MODEL slx_756ac407c6a5
KIND model
CONFIG AbsTol = auto
CONFIG EnableMultiTasking = off
CONFIG FixedStep = SimIn.Environment.Turbulence.dT
CONFIG MaxStep = auto
CONFIG MinStep = auto
CONFIG RelTol = 1e-6
CONFIG SampleTimeConstraint = Unconstrained
CONFIG SolverName = FixedStepAuto
CONFIG StartTime = 0.0
CONFIG StopTime = SimIn.stopTime
BLOCK [SubSystem] Assertions
BLOCK [Clock] Assertions/Clock1
BLOCK [Reference] Assertions/Compare To Constant  REF=simulink/Logic and Bit
Operations/Compare
To Constant
  SourceBlock = simulink/Logic and Bit\nOperations/Compare\nTo Constant
  SourceType = Compare To Constant
BLOCK [Constant] Assertions/Constant2
  Value = SimIn.Switches.TrimModeOn
BLOCK [Constant] Assertions/Constant3
  Value = SimIn.Switches.LinearizeModeOn
BLOCK [Assertion] Assertions/KillifNotSimMode
  AssertionFailFcn = warndlg('Running simulation with TrimMode or LinearizeMode engaged.  Run setup.m to reset.','Warning!')
BLOCK [Logic] Assertions/Logical Operator
  AllPortsSameDT = off
  Operator = NAND
  OutDataTypeStr = boolean
BLOCK [Logic] Assertions/Logical Operator1
  AllPortsSameDT = off
  Operator = OR
  OutDataTypeStr = boolean
BLOCK [BusCreator] Bus Creator
  DisplayOption = bar
  InheritFromInputs = on
  Inputs = 2
  OutDataTypeStr = Bus: BUS_TRIM_INPUT
BLOCK [BusSelector] Bus Selector
  OutputSignals = Vehicle.EOM
BLOCK [BusSelector] Bus Selector1
  OutputAsBus = on
  OutputSignals = AirRelativeData.Veas,AirRelativeData.Vtot,AirRelativeData.alpha,AirRelativeData.beta,WorldRelativeData.gamma,WorldRelativeData.chi,InertialData.Asensed_bIb,AirRelativeData.Vtotdot,AirRelativeData.alphadot,AirRelativeData.betadot,WorldRelativeData.gammadot,WorldRelativeData.chidot,WorldRelativeData.VelDtH_bEh,WorldRelativeData.Euler.phi,WorldRelativeData.Euler.theta,WorldRelativeData.Euler.psi
BLOCK [BusSelector] Bus Selector2
  OutputSignals = InertialData.Pos_bii
BLOCK [BusSelector] Bus Selector5
  OutputSignals = Vehicle.EOM.WorldRelativeData.LatLonAlt.Lon,Vehicle.EOM.WorldRelativeData.LatLonAlt.LatGeod,Vehicle.EOM.WorldRelativeData.LatLonAlt.AltGeod,Vehicle.EOM.WorldRelativeData.Euler,Vehicle.EOM.AirRelativeData.Vcas,Vehicle.EOM.WorldRelativeData.Vel_bEh,Vehicle.EOM.InertialData.Accel_bIi,Vehicle.EOM.WorldRelativeData.AltAGL
BLOCK [BusToVector] Bus to Vector
BLOCK [Demux] Demux
  Outputs = [SimIn.Trim.numEngines SimIn.Trim.numSurfaces]
BLOCK [SubSystem] FlightGear
BLOCK [Inport] FlightGear/Accel_bIi
  Port = 7
BLOCK [Inport] FlightGear/AltAGL
  Port = 8
BLOCK [Inport] FlightGear/AltGeod
  Port = 3
BLOCK [BusSelector] FlightGear/Bus Selector
  OutputSignals = phi,theta,psi
BLOCK [DataTypeConversion] FlightGear/Data Type Conversion1
  OutDataTypeStr = single
  RndMeth = Floor
  SaturateOnIntegerOverflow = off
BLOCK [DataTypeConversion] FlightGear/Data Type Conversion10
  OutDataTypeStr = single
  RndMeth = Floor
  SaturateOnIntegerOverflow = off
BLOCK [DataTypeConversion] FlightGear/Data Type Conversion11
  OutDataTypeStr = single
  RndMeth = Floor
  SaturateOnIntegerOverflow = off
BLOCK [DataTypeConversion] FlightGear/Data Type Conversion12
  OutDataTypeStr = single
  RndMeth = Floor
  SaturateOnIntegerOverflow = off
BLOCK [DataTypeConversion] FlightGear/Data Type Conversion3
  OutDataTypeStr = single
  RndMeth = Floor
  SaturateOnIntegerOverflow = off
BLOCK [DataTypeConversion] FlightGear/Data Type Conversion4
  OutDataTypeStr = single
  RndMeth = Floor
  SaturateOnIntegerOverflow = off
BLOCK [DataTypeConversion] FlightGear/Data Type Conversion5
  OutDataTypeStr = single
  RndMeth = Floor
  SaturateOnIntegerOverflow = off
BLOCK [DataTypeConversion] FlightGear/Data Type Conversion6
  OutDataTypeStr = single
  RndMeth = Floor
  SaturateOnIntegerOverflow = off
BLOCK [DataTypeConversion] FlightGear/Data Type Conversion7
  OutDataTypeStr = single
  RndMeth = Floor
  SaturateOnIntegerOverflow = off
BLOCK [DataTypeConversion] FlightGear/Data Type Conversion8
  OutDataTypeStr = single
  RndMeth = Floor
  SaturateOnIntegerOverflow = off
BLOCK [DataTypeConversion] FlightGear/Data Type Conversion9
  OutDataTypeStr = single
  RndMeth = Floor
  SaturateOnIntegerOverflow = off
BLOCK [Demux] FlightGear/Demux
  Outputs = 3
BLOCK [Demux] FlightGear/Demux1
  Outputs = 3
BLOCK [Inport] FlightGear/Euler
  Port = 4
BLOCK [Inport] FlightGear/LatGeod
  Port = 2
BLOCK [Inport] FlightGear/Long
BLOCK [Reference] FlightGear/Pack net_fdm Packet for FlightGear  REF=aerolibfltsims/Pack
net_fdm Packet
for FlightGear
  AttributesFormatString = Version Selected: %<FlightGearVersion>
  SourceBlock = aerolibfltsims/Pack\nnet_fdm Packet\nfor FlightGear
  SourceType = FlightGearPackNetFdm
BLOCK [Constant] FlightGear/Ref Alt
  NameLocation = left
  Value = 2.65
BLOCK [Sum] FlightGear/Sum
  Inputs = |++
BLOCK [Reference] FlightGear/UDP Send Local  REF=dspnetwork/UDP Send
  LibrarySourceBlock = dspsnks4/UDP Send
  SourceBlock = dspnetwork/UDP Send
  SourceType = UDP Send
BLOCK [Reference] FlightGear/UDP Send Remote  REF=dspnetwork/UDP Send
  LibrarySourceBlock = dspsnks4/UDP Send
  SourceBlock = dspnetwork/UDP Send
  SourceType = UDP Send
BLOCK [Inport] FlightGear/Vcas
  Port = 5
BLOCK [Inport] FlightGear/Vel_bEh
  Port = 6
BLOCK [Gain] FlightGear/ft2m
  Gain = 1/3.281
  NameLocation = top
BLOCK [Gain] FlightGear/ft2m1
  Gain = 1/3.281
  NameLocation = top
BLOCK [Gain] FlightGear/fts2kts
  Gain = 0.3048/1852.0*3600
  NameLocation = top
BLOCK [From] From
  GotoTag = TrimInputs
BLOCK [From] From1
  GotoTag = RefInputs
BLOCK [From] From2
  GotoTag = SimOutputs
BLOCK [From] From3
  GotoTag = EOM
BLOCK [From] From4
  GotoTag = Pos_bii
BLOCK [From] From8
  GotoTag = SimOutputs
BLOCK [SubSystem] GenCtrl Inputs
  Variant = on
  VariantControl = Variant1
BLOCK [SubSystem] GenCtrl Inputs/GL-10 Reference Inputs
  ReferencedSubsystem = GL_10_Reference_Inputs
  VariantControl = GVS_VEH_TYPE_GL10
BLOCK [SubSystem] GenCtrl Inputs/Generic Tilt Rotor Reference Inputs
  ReferencedSubsystem = GTR_Reference_Inputs
  VariantControl = GVS_VEH_TYPE_GTR
BLOCK [SubSystem] GenCtrl Inputs/Generic Tilt Wing Reference Inputs
  ReferencedSubsystem = GTW_Reference_Inputs
  VariantControl = GVS_VEH_TYPE_GTW
BLOCK [SubSystem] GenCtrl Inputs/LA-8 Reference Inputs
  ReferencedSubsystem = LA_8_Reference_Inputs
  VariantControl = GVS_VEH_TYPE_LA8
BLOCK [SubSystem] GenCtrl Inputs/Lift+Cruise Reference Inputs
  ReferencedSubsystem = Lift_Cruise_Reference_Inputs
  VariantControl = GVS_VEH_TYPE_LC
BLOCK [Inport] GenCtrl Inputs/Pos_In
BLOCK [SubSystem] GenCtrl Inputs/Quad6 Reference Inputs
  ReferencedSubsystem = Quad6_Reference_Inputs
  VariantControl = GVS_VEH_TYPE_QUAD6
BLOCK [Outport] GenCtrl Inputs/RefInputs
  OutDataTypeStr = Bus: BUS_REF_INPUT
BLOCK [SubSystem] Global Definitions
BLOCK [Constant] Global Definitions/EOM_IC
  OutDataTypeStr = Bus: BUS_PARAM_EOM
  Value = SimPar.EOM
BLOCK [From] Global Definitions/From
  GotoTag = IC
  TagVisibility = global
BLOCK [From] Global Definitions/From1
  GotoTag = EOM_IC
  TagVisibility = global
BLOCK [Goto] Global Definitions/Goto11
  GotoTag = EOM_IC
  TagVisibility = global
BLOCK [Goto] Global Definitions/Goto3
  GotoTag = IC
  TagVisibility = global
BLOCK [Constant] Global Definitions/IC
  OutDataTypeStr = Bus: BUS_PARAM_IC
  Value = SimPar.IC
BLOCK [Terminator] Global Definitions/Terminator
BLOCK [Terminator] Global Definitions/Terminator1
BLOCK [Goto] Goto
  GotoTag = RefInputs
BLOCK [Goto] Goto1
  GotoTag = SimOutputs
BLOCK [Goto] Goto2
  GotoTag = EOM
BLOCK [Goto] Goto3
  GotoTag = Pos_bii
BLOCK [Goto] Goto4
  GotoTag = TrimInputs
BLOCK [Memory] Memory
BLOCK [Inport] TrimInputs
  SamplingMode = Sample based
  SignalType = real
BLOCK [Outport] TrimOutputs
  OutDataTypeStr = double
  SamplingMode = Sample based
  SignalType = real
  VectorParamsAs1DForOutWhenUnconnected = off
BLOCK [SubSystem] Vehicle Simulation
  ReferencedSubsystem = VehicleSimulationRef
LINE Assertions/Clock1:1 -> Assertions/Compare To Constant:1
LINE Assertions/Compare To Constant:1 -> Assertions/Logical Operator:2
LINE Assertions/Constant2:1 -> Assertions/Logical Operator1:1
LINE Assertions/Constant3:1 -> Assertions/Logical Operator1:2
LINE Assertions/Logical Operator1:1 -> Assertions/Logical Operator:1
LINE Assertions/Logical Operator:1 -> Assertions/KillifNotSimMode:1
LINE Bus Creator:1 -> Goto4:1
LINE Bus Selector1:1 -> Bus to Vector:1
LINE Bus Selector2:1 -> Memory:1
LINE Bus Selector5:1 -> FlightGear:1
LINE Bus Selector5:2 -> FlightGear:2
LINE Bus Selector5:3 -> FlightGear:3
LINE Bus Selector5:4 -> FlightGear:4
LINE Bus Selector5:5 -> FlightGear:5
LINE Bus Selector5:6 -> FlightGear:6
LINE Bus Selector5:7 -> FlightGear:7
LINE Bus Selector5:8 -> FlightGear:8
LINE Bus Selector:1 -> Goto2:1
LINE Bus to Vector:1 -> TrimOutputs:1
LINE Demux:1 -> Bus Creator:1
LINE Demux:2 -> Bus Creator:2
LINE FlightGear/Accel_bIi:1 -> FlightGear/Demux1:1
LINE FlightGear/AltAGL:1 -> FlightGear/ft2m1:1
LINE FlightGear/AltGeod:1 -> FlightGear/ft2m:1
LINE FlightGear/Bus Selector:1 -> FlightGear/Data Type Conversion11:1
LINE FlightGear/Bus Selector:2 -> FlightGear/Data Type Conversion10:1
LINE FlightGear/Bus Selector:3 -> FlightGear/Data Type Conversion9:1
LINE FlightGear/Data Type Conversion10:1 -> FlightGear/Pack net_fdm Packet for FlightGear:5
LINE FlightGear/Data Type Conversion11:1 -> FlightGear/Pack net_fdm Packet for FlightGear:4
LINE FlightGear/Data Type Conversion12:1 -> FlightGear/Pack net_fdm Packet for FlightGear:22
LINE FlightGear/Data Type Conversion1:1 -> FlightGear/Pack net_fdm Packet for FlightGear:25
LINE FlightGear/Data Type Conversion3:1 -> FlightGear/Pack net_fdm Packet for FlightGear:12
LINE FlightGear/Data Type Conversion4:1 -> FlightGear/Pack net_fdm Packet for FlightGear:14
LINE FlightGear/Data Type Conversion5:1 -> FlightGear/Pack net_fdm Packet for FlightGear:15
LINE FlightGear/Data Type Conversion6:1 -> FlightGear/Pack net_fdm Packet for FlightGear:16
LINE FlightGear/Data Type Conversion7:1 -> FlightGear/Pack net_fdm Packet for FlightGear:20
LINE FlightGear/Data Type Conversion8:1 -> FlightGear/Pack net_fdm Packet for FlightGear:21
LINE FlightGear/Data Type Conversion9:1 -> FlightGear/Pack net_fdm Packet for FlightGear:6
LINE FlightGear/Demux1:1 -> FlightGear/Data Type Conversion7:1
LINE FlightGear/Demux1:2 -> FlightGear/Data Type Conversion8:1
LINE FlightGear/Demux1:3 -> FlightGear/Data Type Conversion12:1
LINE FlightGear/Demux:1 -> FlightGear/Data Type Conversion4:1
LINE FlightGear/Demux:2 -> FlightGear/Data Type Conversion5:1
LINE FlightGear/Demux:3 -> FlightGear/Data Type Conversion6:1
LINE FlightGear/Euler:1 -> FlightGear/Bus Selector:1
LINE FlightGear/LatGeod:1 -> FlightGear/Pack net_fdm Packet for FlightGear:2
LINE FlightGear/Long:1 -> FlightGear/Pack net_fdm Packet for FlightGear:1
NET FlightGear/Pack net_fdm Packet for FlightGear:1 -> FlightGear/UDP Send Local:1, FlightGear/UDP Send Remote:1
LINE FlightGear/Ref Alt:1 -> FlightGear/Sum:2
LINE FlightGear/Sum:1 -> FlightGear/Pack net_fdm Packet for FlightGear:3
LINE FlightGear/Vcas:1 -> FlightGear/fts2kts:1
LINE FlightGear/Vel_bEh:1 -> FlightGear/Demux:1
LINE FlightGear/ft2m1:1 -> FlightGear/Data Type Conversion1:1
LINE FlightGear/ft2m:1 -> FlightGear/Sum:1
LINE FlightGear/fts2kts:1 -> FlightGear/Data Type Conversion3:1
LINE From1:1 -> Vehicle Simulation:1
LINE From2:1 -> Bus Selector:1
NET From3:1 -> Bus Selector1:1, Bus Selector2:1
LINE From4:1 -> GenCtrl Inputs:1
LINE From8:1 -> Bus Selector5:1
LINE From:1 -> Vehicle Simulation:2
LINE GenCtrl Inputs:1 -> Goto:1
LINE Global Definitions/EOM_IC:1 -> Global Definitions/Goto11:1
LINE Global Definitions/From1:1 -> Global Definitions/Terminator1:1
LINE Global Definitions/From:1 -> Global Definitions/Terminator:1
LINE Global Definitions/IC:1 -> Global Definitions/Goto3:1
LINE Memory:1 -> Goto3:1
LINE TrimInputs:1 -> Demux:1
LINE Vehicle Simulation:1 -> Goto1:1
note: NET lines group one-source signal fan-out (src -> all destinations, sorted); 1:1 wires keep LINE
